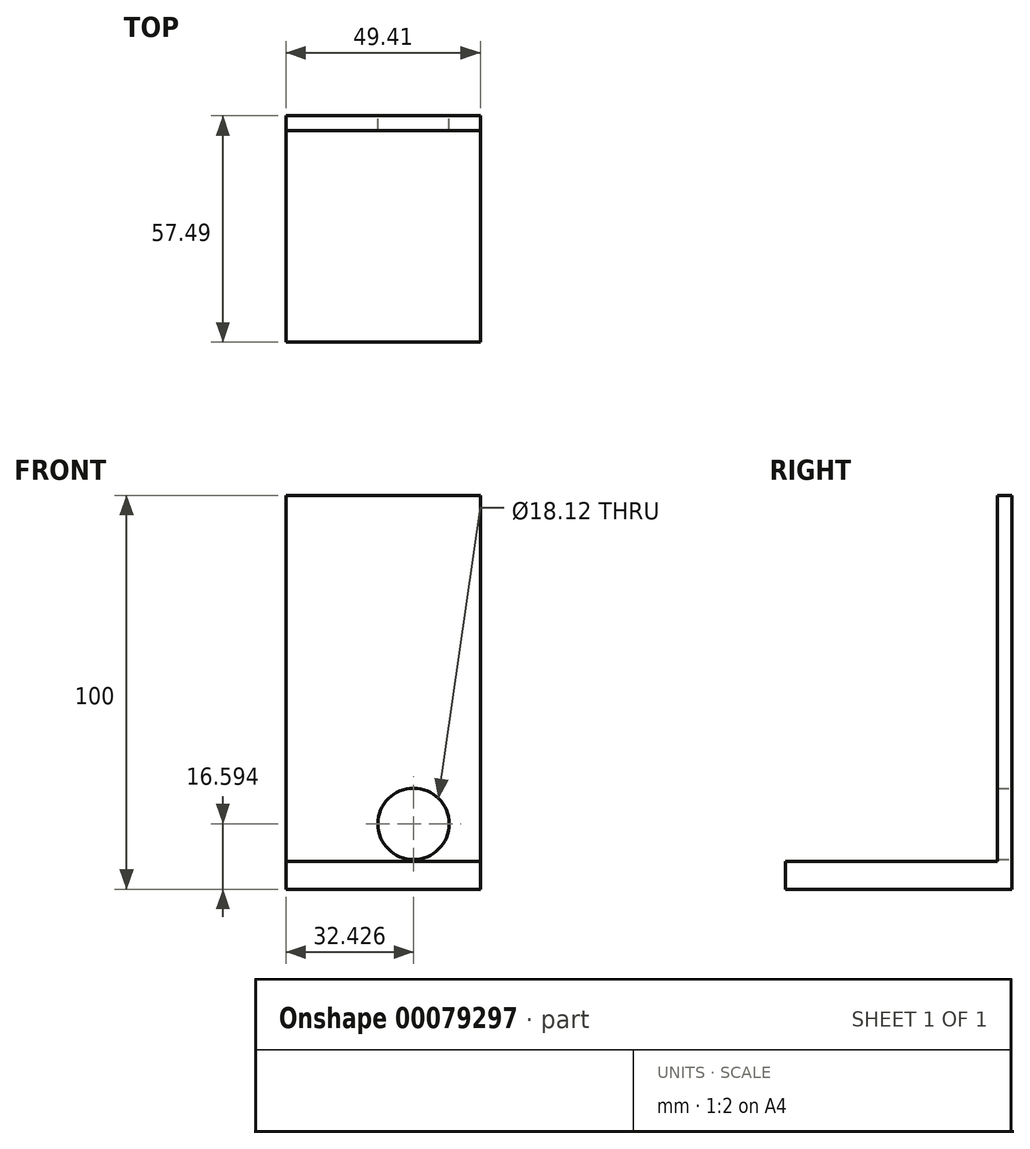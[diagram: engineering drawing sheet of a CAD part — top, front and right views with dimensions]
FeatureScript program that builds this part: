
annotation { "Feature Type Name" : "Feature", "Feature Type Description" : "" }
export const myFeature = defineFeature(function(context is Context, id is Id, definition is map)
    precondition{}
    {
        {
            var Q0;
            Q0=qCreatedBy(makeId("Top.planeOp"),FACE);
            var sketch = newSketch(context, id + "F0", { "sketchPlane" : qUnion([Q0])});
            skLineSegment(sketch, "E0.bottom", {"start": v(0, 0) * mm, "end": v(49.4, 0) * mm});
            skLineSegment(sketch, "E0.top", {"start": v(0, 57.5) * mm, "end": v(49.4, 57.5) * mm});
            skLineSegment(sketch, "E0.left", {"start": v(0, 0) * mm, "end": v(0, 57.5) * mm});
            skLineSegment(sketch, "E0.right", {"start": v(49.4, 0) * mm, "end": v(49.4, 57.5) * mm});
            skSolve(sketch);
        }
        {
            var Q0;
            Q0=makeQuery(id+"F0.imprint","IMPRINT",FACE,{"disambiguationData":[TD([[makeQuery(id+"F0.imprint","IMPRINT",EDGE,{"derivedFrom":sQuery(id+"F0.wireOp",EDGE,"E0.bottom")}),1.0]])]});
            var sketch = newSketch(context, id + "F1", { "sketchPlane" : qUnion([Q0])});
            skLineSegment(sketch, "E1.bottom", {"start": v(0, 57.7) * mm, "end": v(49.41, 57.7) * mm});
            skLineSegment(sketch, "E1.top", {"start": v(0, 53.76) * mm, "end": v(49.41, 53.76) * mm});
            skLineSegment(sketch, "E1.left", {"start": v(0, 57.7) * mm, "end": v(0, 53.76) * mm});
            skLineSegment(sketch, "E1.right", {"start": v(49.41, 57.7) * mm, "end": v(49.41, 53.76) * mm});
            skSolve(sketch);
        }
        {
            var Q0;
            {var subQ5=makeQuery(id+"F0.imprint","IMPRINT",EDGE,{"derivedFrom":sQuery(id+"F0.wireOp",EDGE,"E0.top")});Q0=makeQuery(id+"F1.imprint","IMPRINT",FACE,{"disambiguationData":[TD([[makeQuery(id+"F1.imprint","IMPRINT",EDGE,{"derivedFrom":subQ5}),-1.0]])]});}
            var Q1;
            Q1=sQuery(id+"F1.wireOp",EDGE,"E1.top");
            var Q2;
            Q2=sQuery(id+"F1.wireOp",EDGE,"E1.bottom");
            var Q3;
            Q3=sQuery(id+"F1.wireOp",EDGE,"E1.left");
            var Q4;
            Q4=sQuery(id+"F1.wireOp",EDGE,"E1.right");
            extrude(context, id + "F2", {"entities" : qUnion([Q0]), "surfaceEntities" : qUnion([Q1, Q2, Q3, Q4]), "depth" : 100 * mm});
        }
        {
            var Q0;
            Q0=makeQuery(id+"F0.imprint","IMPRINT",FACE,{"disambiguationData":[TD([[makeQuery(id+"F0.imprint","IMPRINT",EDGE,{"derivedFrom":sQuery(id+"F0.wireOp",EDGE,"E0.bottom")}),1.0]])]});
            var Q1;
            Q1=sQuery(id+"F0.wireOp",EDGE,"E0.right");
            var Q2;
            Q2=sQuery(id+"F0.wireOp",EDGE,"E0.bottom");
            extrude(context, id + "F3", {"entities" : qUnion([Q0]), "operationType" : NewBodyOperationType.ADD, "surfaceEntities" : qUnion([Q1, Q2]), "depth" : 7 * mm});
        }
        {
            var Q0;
            Q0=makeQuery(id+"F2.opExtrude","SWEPT_FACE",FACE,{"disambiguationData":[OSD([sQuery(id+"F0.wireOp",EDGE,"E0.top")])]});
            var sketch = newSketch(context, id + "F4", { "sketchPlane" : qUnion([Q0])});
            skCircle(sketch, "E2", {"center": v(-32.43, 16.6) * mm, "radius": 9.06 * mm});
            skSolve(sketch);
        }
        {
            var Q0;
            Q0 = qSketchRegion(id + "F4", true);
            extrude(context, id + "F5", {"entities" : qUnion([Q0]), "operationType" : NewBodyOperationType.REMOVE, "oppositeDirection" : true, "depth" : 25 * mm});
        }
    });
